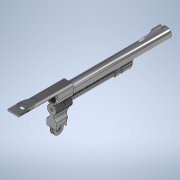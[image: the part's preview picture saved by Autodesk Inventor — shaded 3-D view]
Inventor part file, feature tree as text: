
AUTODESK INVENTOR PART (.ipt)
format: ipt  version: 2021 (Build 250183000, 183)  size: 3,922,432 bytes
history: native  units: mm
features: sketch x55, extrude x53, other x8, pattern_linear x4, fillet x3, pattern_circular x3
ambient origin geometry x8: Origin, YZ Plane, XZ Plane, XY Plane, X Axis, Y Axis, Z Axis, Center Point
bodies: Body1 (feature_tree)
feature tree (126):
  other  "Sólido1"
  extrude  "Extrusão1"  Depth=10.0mm TaperAngle=0.0deg
  extrude  "Extrusão2"  Depth=9.0mm TaperAngle=0.0deg
  extrude  "Extrusão3"  TaperAngle=0.0deg  [1 undecoded]
  extrude  "Extrusão4"  Depth=9.0mm
  extrude  "Extrusão5"  Depth=7.0mm
  extrude  "Extrusão6"  Depth=8.0mm
  extrude  "Extrusão7"  Depth=3.0mm
  extrude  "Extrusão8"  Depth=4.5mm
  extrude  "Extrusão9"  Depth=3.0mm
  extrude  "Extrusão10"  Depth=7.0mm TaperAngle=0.0deg
  extrude  "Extrusão11"  Depth=79.901425mm
  other  "Plano de trabalho1"
  sketch  "Esboço12"  dims[d32=1.0mm d33=0.0mm d34=5.0mm]
  extrude  "Extrusão12"  Depth=5.0mm
  extrude  "Extrusão13"  Depth=2.0mm
  extrude  "Extrusão14"  Depth=1.0mm TaperAngle=0.0deg
  extrude  "Extrusão15"  Depth=2.0mm TaperAngle=0.0deg
  extrude  "Extrusão16"  Depth=5.0mm
  extrude  "Extrusão17"  Depth=2.0mm TaperAngle=0.0deg
  fillet  "Arredondamento3"  Radius=1.0mm
  extrude  "Extrusão19"  TaperAngle=0.0deg  [1 undecoded]
  other  "Plano de trabalho2"
  extrude  "Extrusão20"  Depth=1.0mm TaperAngle=0.0deg
  other  "Plano de trabalho3"
  extrude  "Extrusão22"  Depth=10.0mm
  extrude  "Extrusão23"  Depth=1.0mm TaperAngle=0.0deg
  extrude  "Extrusão24"  Depth=3.5mm TaperAngle=0.0deg
  extrude  "Extrusão25"  [1 undecoded]
  extrude  "Extrusão26"  Depth=3.0mm
  extrude  "Extrusão27"  Depth=3.0mm
  extrude  "Extrusão28"  Depth=4.808mm
  extrude  "Extrusão29"  Depth=9.0mm TaperAngle=0.0deg
  extrude  "Extrusão30"  Depth=4.655mm TaperAngle=0.0deg
  extrude  "Extrusão31"  Depth=21.25mm TaperAngle=0.0deg
  extrude  "Extrusão32"  Depth=0.0009mm TaperAngle=0.0deg
  extrude  "Extrusão33"  Depth=3.7501mm TaperAngle=0.0deg
  extrude  "Extrusão36"  Depth=4.0001mm TaperAngle=0.0deg
  extrude  "Extrusão37"  Depth=3.0mm
  extrude  "Extrusão38"  Depth=1.0mm
  extrude  "Extrusão39"  Depth=9.0mm TaperAngle=0.0deg
  extrude  "Extrusão40"  Depth=9.0mm TaperAngle=0.0deg
  extrude  "Extrusão41"  Depth=3.0mm TaperAngle=0.0deg
  extrude  "Extrusão42"  Depth=1.655mm TaperAngle=0.0deg
  extrude  "Extrusão43"  TaperAngle=0.0deg  [1 undecoded]
  extrude  "Extrusão44"  Depth=2.5mm
  sketch  "Esboço53"  dims[d159=0.5mm d160=0.5mm]
  extrude  "Extrusão48"  Depth=16.0mm
  sketch  "Esboço24"  dims[d62=0.5mm d66=10.0mm]
  fillet  "Arredondamento4"  Radius=2.2mm
  sketch  "Esboço55"  dims[d161=1.5mm]
  sketch  "Esboço56"  dims[d162=0.1mm d163=0.0mm d164=400.0mm d166=1.0mm]
  extrude  "Extrusão49"  Depth=0.5mm
  pattern_linear  "Padrão retangular1"  Count1=40 Spacing1=1.0mm
  other  "Plano de trabalho4"
  extrude  "Extrusão50"  Depth=0.1mm TaperAngle=0.0deg
  pattern_linear  "Padrão retangular2"  Count1=7 Spacing1=0.5mm
  other  "Eixo de trabalho1"
  pattern_circular  "Padrão circular1"  Count=9  [1 undecoded]
  extrude  "Extrusão51"  Depth=0.1mm TaperAngle=0.0deg
  pattern_linear  "Padrão retangular3"  Count1=14 Spacing1=0.5mm
  pattern_circular  "Padrão circular2"  Count=30 Angle=360.0deg
  extrude  "Extrusão52"  Depth=0.5mm TaperAngle=0.0deg
  extrude  "Extrusão53"  Depth=10.0mm TaperAngle=0.0deg
  pattern_linear  "Padrão retangular4"  Spacing1=2.0mm  [1 undecoded]
  other  "Eixo de trabalho2"
  other  "Espiral1"
  pattern_circular  "Padrão circular3"  [2 undecoded]
  extrude  "Extrusão54"  Depth=2.0mm
  extrude  "Extrusão55"  Depth=10.0mm
  extrude  "Extrusão57"  Depth=9.0mm
  extrude  "Extrusão58"  Depth=10.0mm TaperAngle=0.0deg
  fillet  "Arredondamento5"  Radius=2.5mm
  extrude  "Extrusão59"  Depth=10.0mm
  extrude  "Extrusão60"  Depth=10.0mm
  extrude  "Extrusão61"  [1 undecoded]
  sketch  "Esboço1"  dims[d0=10.0mm d1=15.0mm d2=0.0mm]
  sketch  "Esboço2"  dims[d3=9.0mm d4=90.0mm d5=0.0mm]
  sketch  "Esboço3"  dims[d6=7.0mm d7=0.0mm d8=0.0mm]
  sketch  "Esboço4"  dims[d9=8.0mm d10=9.0mm]
  sketch  "Esboço5"  dims[d11=7.0mm d12=0.0mm d13=7.0mm]
  sketch  "Esboço6"  dims[d14=1.0mm d15=0.0mm d16=8.0mm]
  sketch  "Esboço7"  dims[d17=7.0mm d18=0.0mm d19=3.0mm]
  sketch  "Esboço8"  dims[d20=41.5mm d21=0.0mm d22=4.5mm]
  sketch  "Esboço9"  dims[d23=3.0mm d24=0.0mm d25=3.0mm]
  sketch  "Esboço10"  dims[d26=3.0mm d27=0.0mm d28=7.0mm d29=0.0mm]
  sketch  "Esboço11"  dims[d30=11.377725mm d31=79.901425mm]
  sketch  "Esboço14"  dims[d35=20.0mm d37=2.0mm]
  sketch  "Esboço15"  dims[d38=5.0mm d42=1.0mm d43=0.0mm]
  sketch  "Esboço17"  dims[d44=5.0mm d45=2.0mm d46=0.0mm]
  sketch  "Esboço19"  dims[d47=1.5mm d48=5.0mm]
  sketch  "Esboço20"  dims[d49=2.0mm d50=0.0mm d51=0.5mm d52=0.0mm d53=1.0mm]
  sketch  "Esboço22"  dims[d54=9.0mm d55=0.0mm]
  sketch  "Esboço23"  dims[d56=2.5mm d57=0.0mm d58=1.0mm d59=0.0mm]
  sketch  "Esboço25"  dims[d67=43.0mm d68=1.0mm d69=0.0mm]
  sketch  "Esboço26"  dims[d70=-5.0mm d71=3.5mm d72=0.0mm]
  sketch  "Esboço27"  dims[d73=2.5mm d76=-13.0mm]
  sketch  "Esboço28"  dims[d77=1.0mm d78=0.0mm d79=3.0mm]
  sketch  "Esboço29"  dims[d80=1.0mm d81=0.0mm d83=3.0mm]
  sketch  "Esboço30"  dims[d84=4.80844mm d85=4.808mm]
  sketch  "Esboço31"  dims[d86=8.98mm d87=9.0mm d88=0.0mm]
  sketch  "Esboço32"  dims[d89=10.137516mm d90=4.655mm d91=0.0mm]
  sketch  "Esboço34"  dims[d92=4.325mm d93=0.0mm d94=21.25mm d95=0.0mm]
  sketch  "Esboço35"  dims[d96=6.0mm d97=0.0mm d98=0.0009mm d99=0.0mm]
  sketch  "Esboço36"  dims[d100=3.7501mm d101=0.0mm d102=3.7501mm d103=0.0mm]
  sketch  "Esboço37"  dims[d104=4.0001mm d105=0.0mm d106=4.0001mm d107=0.0mm]
  sketch  "Esboço42"  dims[d108=4.0001mm d109=0.0mm d116=3.0mm]
  sketch  "Esboço43"  dims[d117=4.655mm d118=4.325mm d119=0.0mm d120=0.0mm d121=1.0mm]
  sketch  "Esboço44"  dims[d122=9.0mm d123=3.0mm d124=0.0mm]
  sketch  "Esboço45"  dims[d125=3.0mm d126=0.0mm d127=9.0mm d128=0.0mm]
  sketch  "Esboço46"  dims[d129=3.0mm d130=0.0mm d131=3.0mm d132=0.0mm]
  sketch  "Esboço47"  dims[d133=1.655mm d134=1.345mm d135=0.0mm d136=0.0mm d137=1.655mm d138=1.345mm d139=0.0mm d140=0.0mm]
  sketch  "Esboço48"  dims[d141=4.0mm d142=0.0mm d143=0.0mm]
  sketch  "Esboço49"  dims[d151=4.0mm d152=2.5mm]
  sketch  "Esboço50"  dims[d155=16.0mm d156=16.0mm d157=2.2mm d158=0.0mm]
  sketch  "Esboço57"  dims[d167=4.0mm d168=0.1mm d169=0.0mm d170=70.0mm d172=0.5mm d173=90.0mm d175=0.5mm]
  sketch  "Esboço58"  dims[d176=300.0mm d177=360.0deg d182=0.1mm d183=0.0mm d184=140.0mm d186=0.5mm d187=300.0mm d188=360.0deg]
  sketch  "Esboço60"  dims[d190=3.4mm d191=0.0mm d192=0.5mm d193=0.0mm]
  sketch  "Esboço61"  dims[d194=400.0mm d196=1.0mm]
  sketch  "Esboço62"  dims[d197=100.0mm d198=10.0mm d199=30.0mm d200=0.0mm d201=90.0deg d202=90.0deg d203=0.0mm d204=0.0mm d205=60.0mm d206=360.0deg d210=20.0mm d211=0.0mm]
  sketch  "Esboço64"  dims[d212=1.5mm d213=0.0mm]
  sketch  "Esboço65"  dims[d216=1.5mm d217=0.0mm]
  sketch  "Esboço67"  dims[d218=7.0mm d219=0.0mm]
  sketch  "Esboço68"  dims[d220=2.0mm]
  sketch  "Esboço69"  dims[d221=27.0mm]
  sketch  "Esboço70"  dims[d222=7.0mm d223=0.0mm d224=2.0mm d225=1.0mm d226=2.0mm d227=0.5mm d228=9.0mm d229=10.0mm d230=0.0mm d231=2.5mm d232=0.0mm d208=0.5mm d209=0.872665mm]
note: 9 required parameter values undecoded (feature->parameter linkage not recoverable at this tier; creation-order binding heuristic only, values carry confidence <= 0.55)
